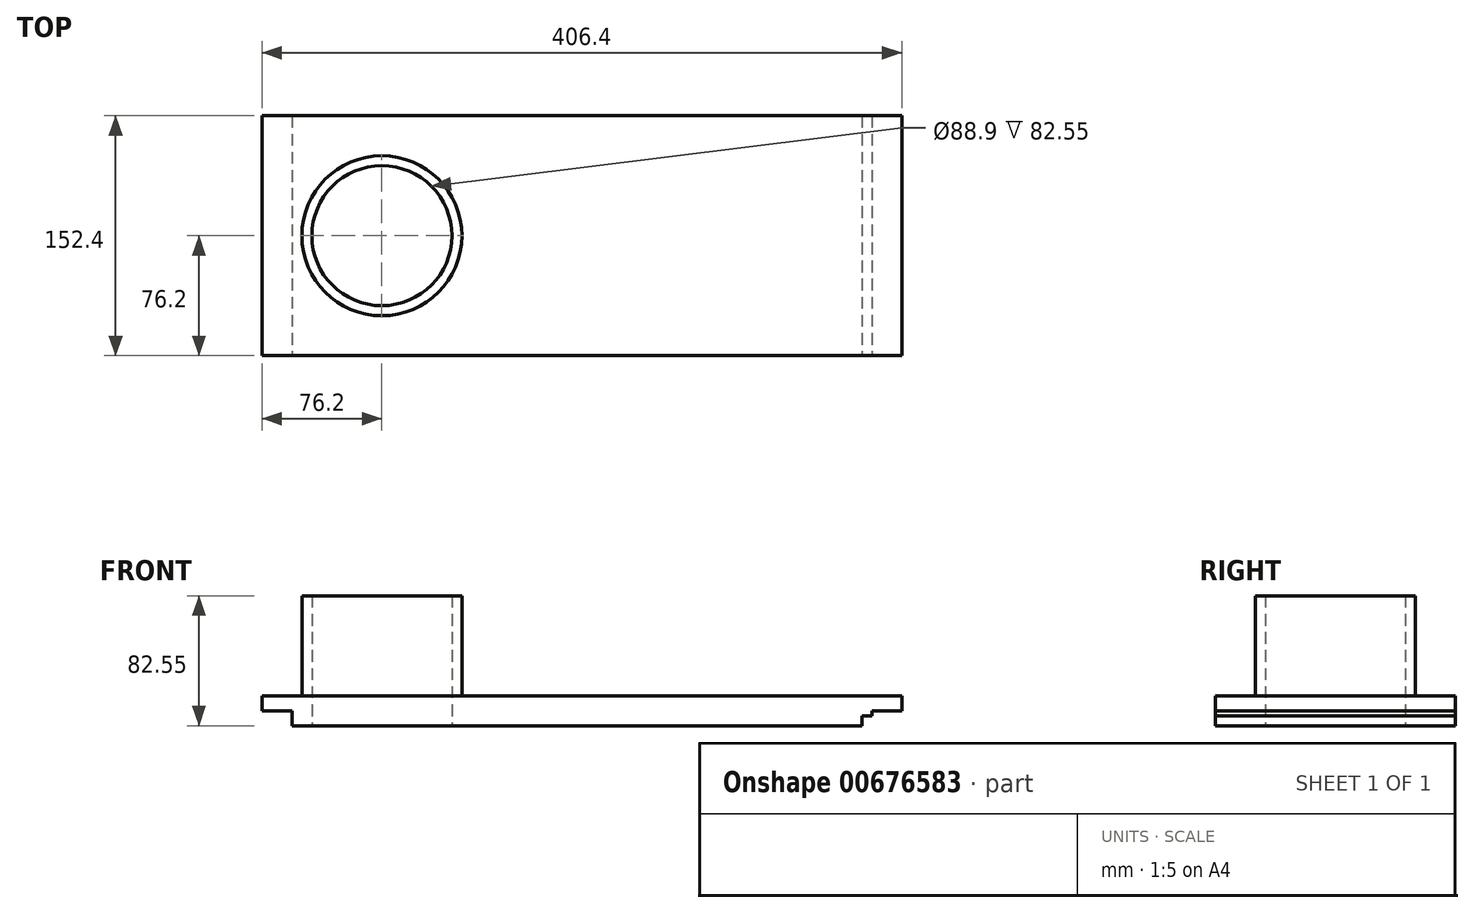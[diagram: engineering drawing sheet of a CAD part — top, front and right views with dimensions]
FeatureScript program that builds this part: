
annotation { "Feature Type Name" : "Feature", "Feature Type Description" : "" }
export const myFeature = defineFeature(function(context is Context, id is Id, definition is map)
    precondition{}
    {
        {
            var Q0;
            Q0=qCreatedBy(makeId("Top.planeOp"),FACE);
            var sketch = newSketch(context, id + "F0", { "sketchPlane" : qUnion([Q0])});
            skLineSegment(sketch, "E0.bottom", {"start": v(-203.2, -76.2) * mm, "end": v(203.2, -76.2) * mm});
            skLineSegment(sketch, "E0.top", {"start": v(-203.2, 76.2) * mm, "end": v(203.2, 76.2) * mm});
            skLineSegment(sketch, "E0.left", {"start": v(-203.2, -76.2) * mm, "end": v(-203.2, 76.2) * mm});
            skLineSegment(sketch, "E0.right", {"start": v(203.2, -76.2) * mm, "end": v(203.2, 76.2) * mm});
            skPoint(sketch, "E0.middle", {"position": v(0, 0) * mm});
            skSolve(sketch);
        }
        {
            var Q0;
            Q0=qSketchRegion(id+"F0",true);
            extrude(context, id + "F1", {"entities" : qUnion([Q0]), "depth" : 19.05 * mm, "offsetDistance" : 25.4 * mm});
        }
        {
            var Q0;
            Q0=makeQuery(id+"F1.opExtrude","SWEPT_FACE",FACE,{"disambiguationData":[OSD([sQuery(id+"F0.wireOp",EDGE,"E0.bottom")])]});
            var sketch = newSketch(context, id + "F2", { "sketchPlane" : qUnion([Q0])});
            skLineSegment(sketch, "E1.bottom", {"start": v(-203.2, 0) * mm, "end": v(-184.15, 0) * mm});
            skLineSegment(sketch, "E1.top", {"start": v(-203.2, 9.53) * mm, "end": v(-184.15, 9.53) * mm});
            skLineSegment(sketch, "E1.left", {"start": v(-203.2, 0) * mm, "end": v(-203.2, 9.52) * mm});
            skLineSegment(sketch, "E1.right", {"start": v(-184.15, 0) * mm, "end": v(-184.15, 9.52) * mm});
            skLineSegment(sketch, "E2.bottom", {"start": v(-184.15, 0) * mm, "end": v(-177.8, 0) * mm});
            skLineSegment(sketch, "E2.top", {"start": v(-184.15, 6.35) * mm, "end": v(-177.8, 6.35) * mm});
            skLineSegment(sketch, "E2.left", {"start": v(-184.15, 0) * mm, "end": v(-184.15, 6.35) * mm});
            skLineSegment(sketch, "E2.right", {"start": v(-177.8, 0) * mm, "end": v(-177.8, 6.35) * mm});
            skLineSegment(sketch, "E3.bottom", {"start": v(203.2, 0) * mm, "end": v(184.15, 0) * mm});
            skLineSegment(sketch, "E3.top", {"start": v(203.2, 9.53) * mm, "end": v(184.15, 9.52) * mm});
            skLineSegment(sketch, "E3.left", {"start": v(203.2, 0) * mm, "end": v(203.2, 9.53) * mm});
            skLineSegment(sketch, "E3.right", {"start": v(184.15, 0) * mm, "end": v(184.15, 9.52) * mm});
            skLineSegment(sketch, "E4.bottom", {"start": v(184.15, 0) * mm, "end": v(177.8, 0) * mm});
            skLineSegment(sketch, "E4.top", {"start": v(184.15, 6.35) * mm, "end": v(177.8, 6.35) * mm});
            skLineSegment(sketch, "E4.left", {"start": v(184.15, 0) * mm, "end": v(184.15, 6.35) * mm});
            skLineSegment(sketch, "E4.right", {"start": v(177.8, 0) * mm, "end": v(177.8, 6.35) * mm});
            skSolve(sketch);
        }
        {
            var Q0;
            Q0=makeQuery(id+"F2.imprint","IMPRINT",FACE,{"disambiguationData":[TD([[makeQuery(id+"F2.imprint","IMPRINT",EDGE,{"derivedFrom":sQuery(id+"F2.wireOp",EDGE,"E1.bottom")}),1.0]])]});
            var Q1;
            Q1=makeQuery(id+"F2.imprint","IMPRINT",FACE,{"disambiguationData":[TD([[makeQuery(id+"F2.imprint","IMPRINT",EDGE,{"derivedFrom":sQuery(id+"F2.wireOp",EDGE,"E3.bottom")}),1.0]])]});
            var Q2;
            Q2=makeQuery(id+"F2.imprint","IMPRINT",FACE,{"disambiguationData":[TD([[makeQuery(id+"F2.imprint","IMPRINT",EDGE,{"derivedFrom":sQuery(id+"F2.wireOp",EDGE,"E4.bottom")}),1.0]])]});
            extrude(context, id + "F3", {"entities" : qUnion([Q0, Q1, Q2]), "operationType" : NewBodyOperationType.REMOVE, "endBound" : BoundingType.THROUGH_ALL, "oppositeDirection" : true, "depth" : 25.4 * mm, "offsetDistance" : 25.4 * mm});
        }
        {
            var Q0;
            Q0=makeQuery(id+"F1.opExtrude","CAP_FACE",FACE,{"disambiguationData":[OSD([sQuery(id+"F0.wireOp",EDGE,"E0.bottom"),sQuery(id+"F0.wireOp",EDGE,"E0.top"),sQuery(id+"F0.wireOp",EDGE,"E0.left"),sQuery(id+"F0.wireOp",EDGE,"E0.right")])],"isStart":true});
            var sketch = newSketch(context, id + "F4", { "sketchPlane" : qUnion([Q0])});
            skCircle(sketch, "E5", {"center": v(0, 0) * mm, "radius": 44.45 * mm});
            skCircle(sketch, "E6", {"center": v(-127, 0) * mm, "radius": 44.45 * mm});
            skCircle(sketch, "E7", {"center": v(127, 0) * mm, "radius": 44.45 * mm});
            skSolve(sketch);
        }
        {
            var Q0;
            Q0=makeQuery(id+"F4.imprint","IMPRINT",FACE,{"disambiguationData":[TD([[makeQuery(id+"F4.imprint","IMPRINT",EDGE,{"derivedFrom":sQuery(id+"F4.wireOp",EDGE,"E6")}),1.0]])]});
            extrude(context, id + "F5", {"entities" : qUnion([Q0]), "operationType" : NewBodyOperationType.REMOVE, "endBound" : BoundingType.THROUGH_ALL, "oppositeDirection" : true, "depth" : 25.4 * mm, "offsetDistance" : 25.4 * mm});
        }
        {
            var Q0;
            Q0=makeQuery(id+"F1.opExtrude","CAP_FACE",FACE,{"disambiguationData":[OSD([sQuery(id+"F0.wireOp",EDGE,"E0.bottom"),sQuery(id+"F0.wireOp",EDGE,"E0.top"),sQuery(id+"F0.wireOp",EDGE,"E0.left"),sQuery(id+"F0.wireOp",EDGE,"E0.right")])],"isStart":false});
            var sketch = newSketch(context, id + "F6", { "sketchPlane" : qUnion([Q0])});
            skCircle(sketch, "E8", {"center": v(-127, 0) * mm, "radius": 50.8 * mm});
            skSolve(sketch);
        }
        {
            var Q0;
            Q0=makeQuery(id+"F6.imprint","IMPRINT",FACE,{"disambiguationData":[TD([[makeQuery(id+"F6.imprint","IMPRINT",EDGE,{"derivedFrom":sQuery(id+"F6.wireOp",EDGE,"E8")}),1.0]])]});
            extrude(context, id + "F7", {"entities" : qUnion([Q0]), "operationType" : NewBodyOperationType.ADD, "depth" : 63.5 * mm, "offsetDistance" : 25.4 * mm});
        }
    });
